# Revit family: RN 80048 Optipress-Aquaplus-Raccordo
name_source: partatom
category: Rohrformteile
units: mm (PartAtom-declared; Revit-internal decimal feet)

## family parameters
Arbeitsebenenbasiert = Nein
Beim Laden mit Abzugskörper schneiden = Nein
Bemaßung runder Anschluss = Durchmesser verwenden
Gemeinsam genutzt = Nein
Immer vertikal = Ja
Teiletyp = Verbindung

## types (13) — shared parameters
1.010.00.2 Number of the part of the guideline = 29
1.010.00.3 Issue date (month) of the guideline = 201308
1.010.00.4 Manufacturer name = R. Nussbaum AG
1.010.00.5 Revision date of the file = 20190521
1.100.00.4 Product designation = Fornitura
1.110.00.2 Index = 4
1.110.00.4 Product designation = Optipress
1.960/3L.00.8 Link (URL) = https://www.nussbaum.ch
29.700.00.4 Product name = Optipress-Aquaplus-Raccordo, con manicotto da pressare
29.700.00.5 Product identification = 2
29.700.00.6 Cross-sectional shape = 1
29.700.00.7 Nominal size system = DN
29.700.00.8 Nominal pressure system = PN
29.710.02.4 Nominal pressure = 16
29.710.02.5 max. allowed overpressure [hPa] = 1600
29.710.02.7 max. allowed continuous operating pressure [hPa] = 1600
29.710.02.9 max. allowed continuous operating temperature [°C] = 95
Connector Visibility = Nein
EnclosingSpace Visibility = Nein

## per-type parameters (varying)
- 80048.21, Optipress-Aquaplus-Raccordo, con manicotto da pressare, DN=15x20, L=37: 1.800.00.3 BS number=01900400000000000000000000000000000000000000000030000000000000000001; 1.810.00.3 Manufacturer’s reference number=80048.21; 1.810.00.4 DATANORM number=80048.21; 1.810.00.5 StLB number=266.382; 1.810.00.6 GTIN number=7612945052230; 29.710.02.10 Fitting weight [kg]=0.067; 29.710.02.3 Designation=Optipress-Aquaplus-Raccordo, con manicotto da pressare, DN=15x20, L=37; CONNECTOR0_DIAMETER_dX_0r=15 mm  [stored 0.0492126 ft]; CONNECTOR0_dX_01=22 mm; CONNECTOR0_ref_dX=22 mm; CONNECTOR1_DIAMETER_dX_0r=20 mm; CONNECTOR1_dX_00=31 mm; CONNECTOR1_dX_01=46 mm; CONNECTOR1_ref_dX=31 mm; R. Nussbaum AG 80048.20 it Visibility=Nein; R. Nussbaum AG 80048.21 it Visibility=Ja; R. Nussbaum AG 80048.22 it Visibility=Nein; R. Nussbaum AG 80048.23 it Visibility=Nein; R. Nussbaum AG 80048.25 it Visibility=Nein; R. Nussbaum AG 80048.27 it Visibility=Nein; R. Nussbaum AG 80048.29 it Visibility=Nein; R. Nussbaum AG 80048.30 it Visibility=Nein; R. Nussbaum AG 80048.31 it Visibility=Nein; R. Nussbaum AG 80048.33 it Visibility=Nein; R. Nussbaum AG 80048.34 it Visibility=Nein; R. Nussbaum AG 80048.35 it Visibility=Nein; R. Nussbaum AG 80048.36 it Visibility=Nein
- 80048.22, Optipress-Aquaplus-Raccordo, con manicotto da pressare, DN=15, L=46: 1.800.00.3 BS number=01900400000000000000000000000000000000000000000030000000000000000002; 1.810.00.3 Manufacturer’s reference number=80048.22; 1.810.00.4 DATANORM number=80048.22; 1.810.00.5 StLB number=266.383; 1.810.00.6 GTIN number=7612945052247; 29.710.02.10 Fitting weight [kg]=0.057; 29.710.02.3 Designation=Optipress-Aquaplus-Raccordo, con manicotto da pressare, DN=15, L=46; CONNECTOR0_DIAMETER_dX_0r=15 mm  [stored 0.0492126 ft]; CONNECTOR0_dX_01=22 mm; CONNECTOR0_ref_dX=22 mm; CONNECTOR1_DIAMETER_dX_0r=15 mm  [stored 0.0492126 ft]; CONNECTOR1_dX_00=39 mm; CONNECTOR1_dX_01=52 mm; CONNECTOR1_ref_dX=39 mm; R. Nussbaum AG 80048.20 it Visibility=Nein; R. Nussbaum AG 80048.21 it Visibility=Nein; R. Nussbaum AG 80048.22 it Visibility=Ja; R. Nussbaum AG 80048.23 it Visibility=Nein; R. Nussbaum AG 80048.25 it Visibility=Nein; R. Nussbaum AG 80048.27 it Visibility=Nein; R. Nussbaum AG 80048.29 it Visibility=Nein; R. Nussbaum AG 80048.30 it Visibility=Nein; R. Nussbaum AG 80048.31 it Visibility=Nein; R. Nussbaum AG 80048.33 it Visibility=Nein; R. Nussbaum AG 80048.34 it Visibility=Nein; R. Nussbaum AG 80048.35 it Visibility=Nein; R. Nussbaum AG 80048.36 it Visibility=Nein
- 80048.23, Optipress-Aquaplus-Raccordo, con manicotto da pressare, DN=15x20, L=37: 1.800.00.3 BS number=01900400000000000000000000000000000000000000000030000000000000000003; 1.810.00.3 Manufacturer’s reference number=80048.23; 1.810.00.4 DATANORM number=80048.23; 1.810.00.5 StLB number=266.383; 1.810.00.6 GTIN number=7612945052254; 29.710.02.10 Fitting weight [kg]=0.068; 29.710.02.3 Designation=Optipress-Aquaplus-Raccordo, con manicotto da pressare, DN=15x20, L=37; CONNECTOR0_DIAMETER_dX_0r=15 mm  [stored 0.0492126 ft]; CONNECTOR0_dX_01=22 mm; CONNECTOR0_ref_dX=22 mm; CONNECTOR1_DIAMETER_dX_0r=20 mm; CONNECTOR1_dX_00=30 mm; CONNECTOR1_dX_01=45 mm; CONNECTOR1_ref_dX=30 mm; R. Nussbaum AG 80048.20 it Visibility=Nein; R. Nussbaum AG 80048.21 it Visibility=Nein; R. Nussbaum AG 80048.22 it Visibility=Nein; R. Nussbaum AG 80048.23 it Visibility=Ja; R. Nussbaum AG 80048.25 it Visibility=Nein; R. Nussbaum AG 80048.27 it Visibility=Nein; R. Nussbaum AG 80048.29 it Visibility=Nein; R. Nussbaum AG 80048.30 it Visibility=Nein; R. Nussbaum AG 80048.31 it Visibility=Nein; R. Nussbaum AG 80048.33 it Visibility=Nein; R. Nussbaum AG 80048.34 it Visibility=Nein; R. Nussbaum AG 80048.35 it Visibility=Nein; R. Nussbaum AG 80048.36 it Visibility=Nein
- 80048.25, Optipress-Aquaplus-Raccordo, con manicotto da pressare, DN=20, L=46: 1.800.00.3 BS number=01900400000000000000000000000000000000000000000030000000000000000004; 1.810.00.3 Manufacturer’s reference number=80048.25; 1.810.00.4 DATANORM number=80048.25; 1.810.00.5 StLB number=266.384; 1.810.00.6 GTIN number=7612945052261; 29.710.02.10 Fitting weight [kg]=0.08; 29.710.02.3 Designation=Optipress-Aquaplus-Raccordo, con manicotto da pressare, DN=20, L=46; CONNECTOR0_DIAMETER_dX_0r=20 mm; CONNECTOR0_dX_01=24 mm  [stored 0.0787402 ft]; CONNECTOR0_ref_dX=24 mm  [stored 0.0787402 ft]; CONNECTOR1_DIAMETER_dX_0r=20 mm; CONNECTOR1_dX_00=39 mm; CONNECTOR1_dX_01=54 mm; CONNECTOR1_ref_dX=39 mm; R. Nussbaum AG 80048.20 it Visibility=Nein; R. Nussbaum AG 80048.21 it Visibility=Nein; R. Nussbaum AG 80048.22 it Visibility=Nein; R. Nussbaum AG 80048.23 it Visibility=Nein; R. Nussbaum AG 80048.25 it Visibility=Ja; R. Nussbaum AG 80048.27 it Visibility=Nein; R. Nussbaum AG 80048.29 it Visibility=Nein; R. Nussbaum AG 80048.30 it Visibility=Nein; R. Nussbaum AG 80048.31 it Visibility=Nein; R. Nussbaum AG 80048.33 it Visibility=Nein; R. Nussbaum AG 80048.34 it Visibility=Nein; R. Nussbaum AG 80048.35 it Visibility=Nein; R. Nussbaum AG 80048.36 it Visibility=Nein
- 80048.27, Optipress-Aquaplus-Raccordo, con manicotto da pressare, DN=20x25, L=40: 1.800.00.3 BS number=01900400000000000000000000000000000000000000000030000000000000000005; 1.810.00.3 Manufacturer’s reference number=80048.27; 1.810.00.4 DATANORM number=80048.27; 1.810.00.5 StLB number=266.384; 1.810.00.6 GTIN number=7612945052278; 29.710.02.10 Fitting weight [kg]=0.1; 29.710.02.3 Designation=Optipress-Aquaplus-Raccordo, con manicotto da pressare, DN=20x25, L=40; CONNECTOR0_DIAMETER_dX_0r=20 mm; CONNECTOR0_dX_01=24 mm  [stored 0.0787402 ft]; CONNECTOR0_ref_dX=24 mm  [stored 0.0787402 ft]; CONNECTOR1_DIAMETER_dX_0r=25 mm  [stored 0.082021 ft]; CONNECTOR1_dX_00=31 mm; CONNECTOR1_dX_01=48 mm; CONNECTOR1_ref_dX=31 mm; R. Nussbaum AG 80048.20 it Visibility=Nein; R. Nussbaum AG 80048.21 it Visibility=Nein; R. Nussbaum AG 80048.22 it Visibility=Nein; R. Nussbaum AG 80048.23 it Visibility=Nein; R. Nussbaum AG 80048.25 it Visibility=Nein; R. Nussbaum AG 80048.27 it Visibility=Ja; R. Nussbaum AG 80048.29 it Visibility=Nein; R. Nussbaum AG 80048.30 it Visibility=Nein; R. Nussbaum AG 80048.31 it Visibility=Nein; R. Nussbaum AG 80048.33 it Visibility=Nein; R. Nussbaum AG 80048.34 it Visibility=Nein; R. Nussbaum AG 80048.35 it Visibility=Nein; R. Nussbaum AG 80048.36 it Visibility=Nein
- 80048.29, Optipress-Aquaplus-Raccordo, con manicotto da pressare, DN=25, L=48: 1.800.00.3 BS number=01900400000000000000000000000000000000000000000030000000000000000006; 1.810.00.3 Manufacturer’s reference number=80048.29; 1.810.00.4 DATANORM number=80048.29; 1.810.00.5 StLB number=266.385; 1.810.00.6 GTIN number=7612945052285; 29.710.02.10 Fitting weight [kg]=0.122; 29.710.02.3 Designation=Optipress-Aquaplus-Raccordo, con manicotto da pressare, DN=25, L=48; CONNECTOR0_DIAMETER_dX_0r=25 mm  [stored 0.082021 ft]; CONNECTOR0_dX_01=24 mm  [stored 0.0787402 ft]; CONNECTOR0_ref_dX=24 mm  [stored 0.0787402 ft]; CONNECTOR1_DIAMETER_dX_0r=25 mm  [stored 0.082021 ft]; CONNECTOR1_dX_00=39 mm; CONNECTOR1_dX_01=56 mm; CONNECTOR1_ref_dX=39 mm; R. Nussbaum AG 80048.20 it Visibility=Nein; R. Nussbaum AG 80048.21 it Visibility=Nein; R. Nussbaum AG 80048.22 it Visibility=Nein; R. Nussbaum AG 80048.23 it Visibility=Nein; R. Nussbaum AG 80048.25 it Visibility=Nein; R. Nussbaum AG 80048.27 it Visibility=Nein; R. Nussbaum AG 80048.29 it Visibility=Ja; R. Nussbaum AG 80048.30 it Visibility=Nein; R. Nussbaum AG 80048.31 it Visibility=Nein; R. Nussbaum AG 80048.33 it Visibility=Nein; R. Nussbaum AG 80048.34 it Visibility=Nein; R. Nussbaum AG 80048.35 it Visibility=Nein; R. Nussbaum AG 80048.36 it Visibility=Nein
- 80048.31, Optipress-Aquaplus-Raccordo, con manicotto da pressare, DN=32, L=43: 1.800.00.3 BS number=01900400000000000000000000000000000000000000000030000000000000000007; 1.810.00.3 Manufacturer’s reference number=80048.31; 1.810.00.4 DATANORM number=80048.31; 1.810.00.5 StLB number=266.386; 1.810.00.6 GTIN number=7612945052308; 29.710.02.10 Fitting weight [kg]=0.195; 29.710.02.3 Designation=Optipress-Aquaplus-Raccordo, con manicotto da pressare, DN=32, L=43; CONNECTOR0_DIAMETER_dX_0r=32 mm; CONNECTOR0_dX_01=26 mm; CONNECTOR0_ref_dX=26 mm; CONNECTOR1_DIAMETER_dX_0r=40 mm; CONNECTOR1_dX_00=36 mm; CONNECTOR1_dX_01=55 mm; CONNECTOR1_ref_dX=36 mm; R. Nussbaum AG 80048.20 it Visibility=Nein; R. Nussbaum AG 80048.21 it Visibility=Nein; R. Nussbaum AG 80048.22 it Visibility=Nein; R. Nussbaum AG 80048.23 it Visibility=Nein; R. Nussbaum AG 80048.25 it Visibility=Nein; R. Nussbaum AG 80048.27 it Visibility=Nein; R. Nussbaum AG 80048.29 it Visibility=Nein; R. Nussbaum AG 80048.30 it Visibility=Nein; R. Nussbaum AG 80048.31 it Visibility=Ja; R. Nussbaum AG 80048.33 it Visibility=Nein; R. Nussbaum AG 80048.34 it Visibility=Nein; R. Nussbaum AG 80048.35 it Visibility=Nein; R. Nussbaum AG 80048.36 it Visibility=Nein
- 80048.33, Optipress-Aquaplus-Raccordo, con manicotto da pressare, DN=40, L=58: 1.800.00.3 BS number=01900400000000000000000000000000000000000000000030000000000000000008; 1.810.00.3 Manufacturer’s reference number=80048.33; 1.810.00.4 DATANORM number=80048.33; 1.810.00.5 StLB number=266.387; 1.810.00.6 GTIN number=7612945052315; 29.710.02.10 Fitting weight [kg]=0.3; 29.710.02.3 Designation=Optipress-Aquaplus-Raccordo, con manicotto da pressare, DN=40, L=58; CONNECTOR0_DIAMETER_dX_0r=40 mm; CONNECTOR0_dX_01=36 mm; CONNECTOR0_ref_dX=36 mm; CONNECTOR1_DIAMETER_dX_0r=40 mm; CONNECTOR1_dX_00=50 mm; CONNECTOR1_dX_01=69 mm; CONNECTOR1_ref_dX=50 mm; R. Nussbaum AG 80048.20 it Visibility=Nein; R. Nussbaum AG 80048.21 it Visibility=Nein; R. Nussbaum AG 80048.22 it Visibility=Nein; R. Nussbaum AG 80048.23 it Visibility=Nein; R. Nussbaum AG 80048.25 it Visibility=Nein; R. Nussbaum AG 80048.27 it Visibility=Nein; R. Nussbaum AG 80048.29 it Visibility=Nein; R. Nussbaum AG 80048.30 it Visibility=Nein; R. Nussbaum AG 80048.31 it Visibility=Nein; R. Nussbaum AG 80048.33 it Visibility=Ja; R. Nussbaum AG 80048.34 it Visibility=Nein; R. Nussbaum AG 80048.35 it Visibility=Nein; R. Nussbaum AG 80048.36 it Visibility=Nein
- 80048.34, Optipress-Aquaplus-Raccordo, con manicotto da pressare, DN=40x32, L=60: 1.800.00.3 BS number=01900400000000000000000000000000000000000000000030000000000000000009; 1.810.00.3 Manufacturer’s reference number=80048.34; 1.810.00.4 DATANORM number=80048.34; 1.810.00.5 StLB number=266.387; 1.810.00.6 GTIN number=7612945052322; 29.710.02.10 Fitting weight [kg]=0.33; 29.710.02.3 Designation=Optipress-Aquaplus-Raccordo, con manicotto da pressare, DN=40x32, L=60; CONNECTOR0_DIAMETER_dX_0r=40 mm; CONNECTOR0_dX_01=36 mm; CONNECTOR0_ref_dX=36 mm; CONNECTOR1_DIAMETER_dX_0r=50 mm; CONNECTOR1_dX_00=49 mm; CONNECTOR1_dX_01=73 mm; CONNECTOR1_ref_dX=49 mm; R. Nussbaum AG 80048.20 it Visibility=Nein; R. Nussbaum AG 80048.21 it Visibility=Nein; R. Nussbaum AG 80048.22 it Visibility=Nein; R. Nussbaum AG 80048.23 it Visibility=Nein; R. Nussbaum AG 80048.25 it Visibility=Nein; R. Nussbaum AG 80048.27 it Visibility=Nein; R. Nussbaum AG 80048.29 it Visibility=Nein; R. Nussbaum AG 80048.30 it Visibility=Nein; R. Nussbaum AG 80048.31 it Visibility=Nein; R. Nussbaum AG 80048.33 it Visibility=Nein; R. Nussbaum AG 80048.34 it Visibility=Ja; R. Nussbaum AG 80048.35 it Visibility=Nein; R. Nussbaum AG 80048.36 it Visibility=Nein
- 80048.35, Optipress-Aquaplus-Raccordo, con manicotto da pressare, DN=50, L=63: 1.800.00.3 BS number=01900400000000000000000000000000000000000000000030000000000000000010; 1.810.00.3 Manufacturer’s reference number=80048.35; 1.810.00.4 DATANORM number=80048.35; 1.810.00.5 StLB number=266.388; 1.810.00.6 GTIN number=7612945052339; 29.710.02.10 Fitting weight [kg]=0.526; 29.710.02.3 Designation=Optipress-Aquaplus-Raccordo, con manicotto da pressare, DN=50, L=63; CONNECTOR0_DIAMETER_dX_0r=50 mm; CONNECTOR0_dX_01=40 mm; CONNECTOR0_ref_dX=40 mm; CONNECTOR1_DIAMETER_dX_0r=50 mm; CONNECTOR1_dX_00=53 mm; CONNECTOR1_dX_01=77 mm  [stored 0.252625 ft]; CONNECTOR1_ref_dX=53 mm; R. Nussbaum AG 80048.20 it Visibility=Nein; R. Nussbaum AG 80048.21 it Visibility=Nein; R. Nussbaum AG 80048.22 it Visibility=Nein; R. Nussbaum AG 80048.23 it Visibility=Nein; R. Nussbaum AG 80048.25 it Visibility=Nein; R. Nussbaum AG 80048.27 it Visibility=Nein; R. Nussbaum AG 80048.29 it Visibility=Nein; R. Nussbaum AG 80048.30 it Visibility=Nein; R. Nussbaum AG 80048.31 it Visibility=Nein; R. Nussbaum AG 80048.33 it Visibility=Nein; R. Nussbaum AG 80048.34 it Visibility=Nein; R. Nussbaum AG 80048.35 it Visibility=Ja; R. Nussbaum AG 80048.36 it Visibility=Nein
- 80048.36, Optipress-Aquaplus-Raccordo, con manicotto da pressare, DN=50x65, L=66: 1.800.00.3 BS number=01900400000000000000000000000000000000000000000030000000000000000011; 1.810.00.3 Manufacturer’s reference number=80048.36; 1.810.00.4 DATANORM number=80048.36; 1.810.00.5 StLB number=266.388; 1.810.00.6 GTIN number=7612945052346; 29.710.02.10 Fitting weight [kg]=0.655; 29.710.02.3 Designation=Optipress-Aquaplus-Raccordo, con manicotto da pressare, DN=50x65, L=66; CONNECTOR0_DIAMETER_dX_0r=50 mm; CONNECTOR0_dX_01=40 mm; CONNECTOR0_ref_dX=40 mm; CONNECTOR1_DIAMETER_dX_0r=65 mm; CONNECTOR1_dX_00=54 mm; CONNECTOR1_dX_01=81 mm; CONNECTOR1_ref_dX=54 mm; R. Nussbaum AG 80048.20 it Visibility=Nein; R. Nussbaum AG 80048.21 it Visibility=Nein; R. Nussbaum AG 80048.22 it Visibility=Nein; R. Nussbaum AG 80048.23 it Visibility=Nein; R. Nussbaum AG 80048.25 it Visibility=Nein; R. Nussbaum AG 80048.27 it Visibility=Nein; R. Nussbaum AG 80048.29 it Visibility=Nein; R. Nussbaum AG 80048.30 it Visibility=Nein; R. Nussbaum AG 80048.31 it Visibility=Nein; R. Nussbaum AG 80048.33 it Visibility=Nein; R. Nussbaum AG 80048.34 it Visibility=Nein; R. Nussbaum AG 80048.35 it Visibility=Nein; R. Nussbaum AG 80048.36 it Visibility=Ja
- 80048.20, Optipress-Aquaplus-Raccordo, con manicotto da pressare, DN=12x15, L=43: 1.800.00.3 BS number=01900400000000000000000000000000000000000000000030000000000000000034; 1.810.00.3 Manufacturer’s reference number=80048.20; 1.810.00.4 DATANORM number=80048.20; 1.810.00.5 StLB number=266.382; 1.810.00.6 GTIN number=7612945052223; 29.710.02.10 Fitting weight [kg]=0.047; 29.710.02.3 Designation=Optipress-Aquaplus-Raccordo, con manicotto da pressare, DN=12x15, L=43; CONNECTOR0_DIAMETER_dX_0r=12 mm  [stored 0.0393701 ft]; CONNECTOR0_dX_01=22 mm; CONNECTOR0_ref_dX=22 mm; CONNECTOR1_DIAMETER_dX_0r=15 mm  [stored 0.0492126 ft]; CONNECTOR1_dX_00=37 mm; CONNECTOR1_dX_01=50 mm; CONNECTOR1_ref_dX=37 mm; R. Nussbaum AG 80048.20 it Visibility=Ja; R. Nussbaum AG 80048.21 it Visibility=Nein; R. Nussbaum AG 80048.22 it Visibility=Nein; R. Nussbaum AG 80048.23 it Visibility=Nein; R. Nussbaum AG 80048.25 it Visibility=Nein; R. Nussbaum AG 80048.27 it Visibility=Nein; R. Nussbaum AG 80048.29 it Visibility=Nein; R. Nussbaum AG 80048.30 it Visibility=Nein; R. Nussbaum AG 80048.31 it Visibility=Nein; R. Nussbaum AG 80048.33 it Visibility=Nein; R. Nussbaum AG 80048.34 it Visibility=Nein; R. Nussbaum AG 80048.35 it Visibility=Nein; R. Nussbaum AG 80048.36 it Visibility=Nein
- 80048.30, Optipress-Aquaplus-Raccordo, con manicotto da pressare, DN=25x32, L=42: 1.800.00.3 BS number=01900400000000000000000000000000000000000000000030000000000000000035; 1.810.00.3 Manufacturer’s reference number=80048.30; 1.810.00.4 DATANORM number=80048.30; 1.810.00.5 StLB number=266.385; 1.810.00.6 GTIN number=7612945052292; 29.710.02.10 Fitting weight [kg]=0.147; 29.710.02.3 Designation=Optipress-Aquaplus-Raccordo, con manicotto da pressare, DN=25x32, L=42; CONNECTOR0_DIAMETER_dX_0r=25 mm  [stored 0.082021 ft]; CONNECTOR0_dX_01=24 mm  [stored 0.0787402 ft]; CONNECTOR0_ref_dX=24 mm  [stored 0.0787402 ft]; CONNECTOR1_DIAMETER_dX_0r=32 mm; CONNECTOR1_dX_00=33 mm; CONNECTOR1_dX_01=52 mm; CONNECTOR1_ref_dX=33 mm; R. Nussbaum AG 80048.20 it Visibility=Nein; R. Nussbaum AG 80048.21 it Visibility=Nein; R. Nussbaum AG 80048.22 it Visibility=Nein; R. Nussbaum AG 80048.23 it Visibility=Nein; R. Nussbaum AG 80048.25 it Visibility=Nein; R. Nussbaum AG 80048.27 it Visibility=Nein; R. Nussbaum AG 80048.29 it Visibility=Nein; R. Nussbaum AG 80048.30 it Visibility=Ja; R. Nussbaum AG 80048.31 it Visibility=Nein; R. Nussbaum AG 80048.33 it Visibility=Nein; R. Nussbaum AG 80048.34 it Visibility=Nein; R. Nussbaum AG 80048.35 it Visibility=Nein; R. Nussbaum AG 80048.36 it Visibility=Nein

note: column(s) folded — value = type name in every type: 1.800.00.4 Comment field

note: [stored X ft] marks values corroborated as IEEE doubles in the binary element streams (Revit-internal decimal feet)

## geometry (parser evidence)
native form markers: Sweep x3
no freeform markers — native parametric forms only
